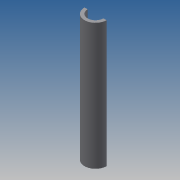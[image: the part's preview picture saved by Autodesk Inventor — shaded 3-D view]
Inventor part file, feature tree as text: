
AUTODESK INVENTOR PART (.ipt)
format: ipt  version: 2014 SP1 (Build 180222100, 222)  size: 69,632 bytes
history: native  units: in
note: dims shown in document units (in); Inventor stores cm internally (conversion verified against a paired STEP export)
features: extrude x1, sketch x1
ambient origin geometry x8: Origin, YZ Plane, XZ Plane, XY Plane, X Axis, Y Axis, Z Axis, Center Point
bodies: Solid1 (feature_tree)
feature tree (2):
  extrude  "Extrusion1"  Depth=4.0in
  sketch  "Sketch1"  dims[d0=0.7in d1=0.1in d2=4.0in d3=0.0in]
